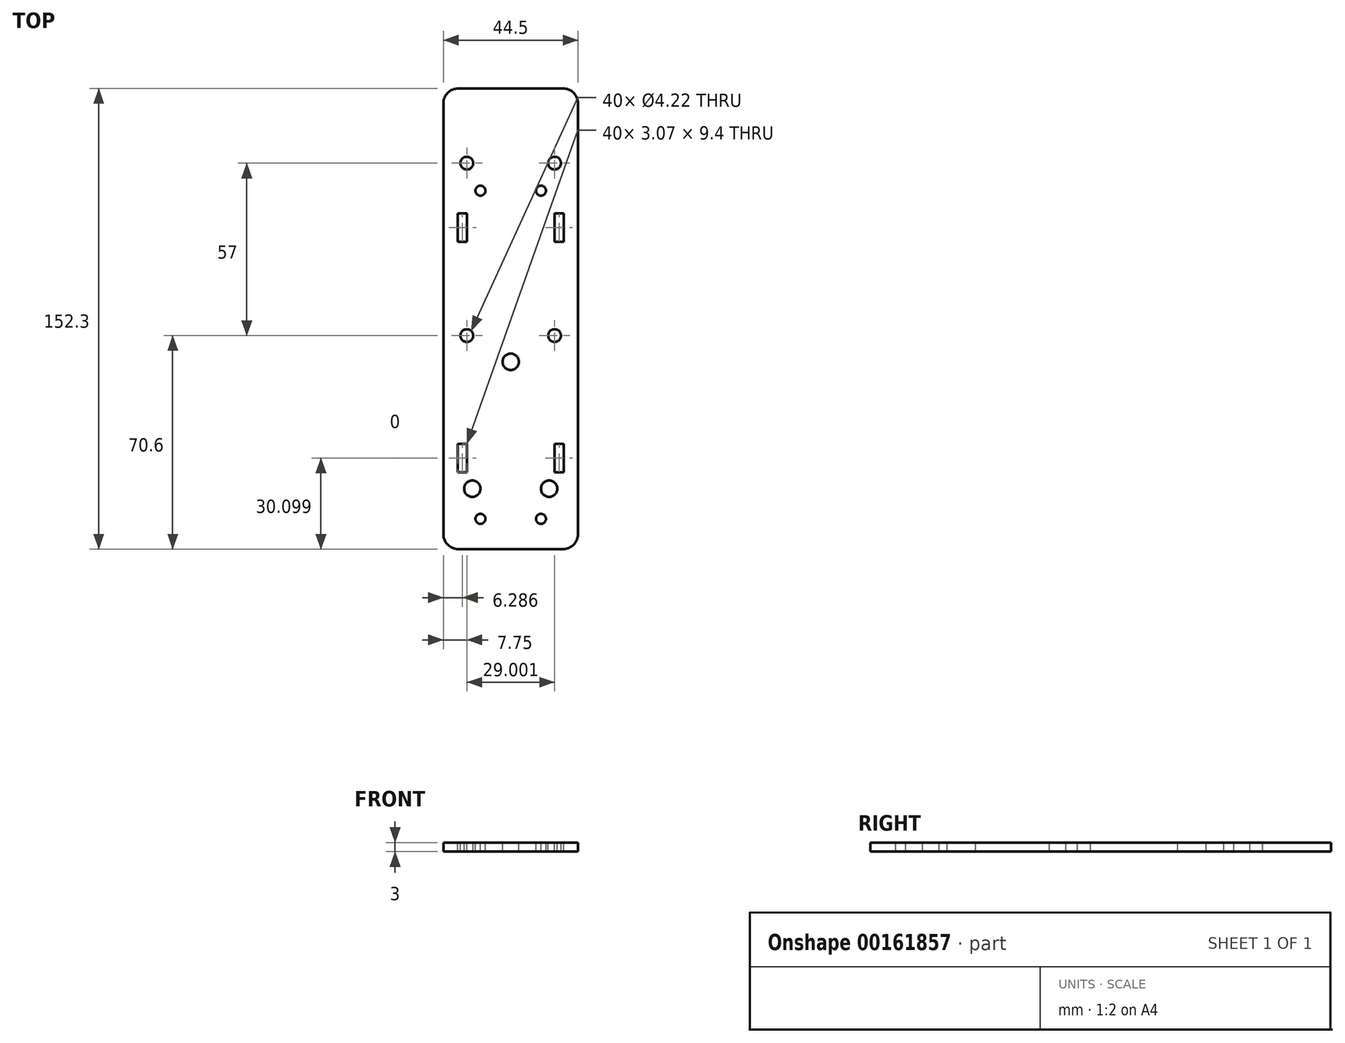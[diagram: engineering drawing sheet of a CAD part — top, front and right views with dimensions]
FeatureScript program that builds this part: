
annotation { "Feature Type Name" : "Feature", "Feature Type Description" : "" }
export const myFeature = defineFeature(function(context is Context, id is Id, definition is map)
    precondition{}
    {
        {
            var Q0;
            Q0=qCreatedBy(makeId("Top.planeOp"),FACE);
            var sketch = newSketch(context, id + "F0", { "sketchPlane" : qUnion([Q0])});
            skLineSegment(sketch, "E0.bottom", {"start": v(17.25, -78) * mm, "end": v(-17.25, -78) * mm});
            skLineSegment(sketch, "E0.top", {"start": v(17.25, 78) * mm, "end": v(-17.25, 78) * mm});
            skLineSegment(sketch, "E0.left", {"start": v(22.25, -73) * mm, "end": v(22.25, 73) * mm});
            skLineSegment(sketch, "E0.right", {"start": v(-22.25, -73) * mm, "end": v(-22.25, 73) * mm});
            skPoint(sketch, "E0.middle", {"position": v(0, 0) * mm});
            skPoint(sketch, "E1.visualSharp", {"position": v(-22.25, -78) * mm});
            skArc(sketch, "E1.filletArc", {"start": v(-22.25, -73) * mm, "mid": v(-20.79, -76.54) * mm, "end": v(-17.25, -78) * mm});
            skPoint(sketch, "E2.visualSharp", {"position": v(22.25, -78) * mm});
            skArc(sketch, "E2.filletArc", {"start": v(17.25, -78) * mm, "mid": v(20.79, -76.54) * mm, "end": v(22.25, -73) * mm});
            skPoint(sketch, "E3.visualSharp", {"position": v(-22.25, 78) * mm});
            skArc(sketch, "E3.filletArc", {"start": v(-17.25, 78) * mm, "mid": v(-20.79, 76.54) * mm, "end": v(-22.25, 73) * mm});
            skPoint(sketch, "E4.visualSharp", {"position": v(22.25, 78) * mm});
            skArc(sketch, "E4.filletArc", {"start": v(22.25, 73) * mm, "mid": v(20.79, 76.54) * mm, "end": v(17.25, 78) * mm});
            skSolve(sketch);
        }
        {
            var Q0;
            Q0=qSketchRegion(id+"F0",true);
            extrude(context, id + "F1", {"entities" : qUnion([Q0]), "oppositeDirection" : true, "depth" : 3 * mm});
        }
        {
            var Q0;
            Q0=makeQuery(id+"F1.opExtrude","CAP_FACE",FACE,{"disambiguationData":[OSD([sQuery(id+"F0.wireOp",EDGE,"E0.bottom"),sQuery(id+"F0.wireOp",EDGE,"E0.top"),sQuery(id+"F0.wireOp",EDGE,"E0.left"),sQuery(id+"F0.wireOp",EDGE,"E0.right"),sQuery(id+"F0.wireOp",EDGE,"E1.filletArc"),sQuery(id+"F0.wireOp",EDGE,"E2.filletArc"),sQuery(id+"F0.wireOp",EDGE,"E3.filletArc"),sQuery(id+"F0.wireOp",EDGE,"E4.filletArc")])],"isStart":true});
            var sketch = newSketch(context, id + "F2", { "sketchPlane" : qUnion([Q0])});
            skLineSegment(sketch, "E5.0", {"start": v(17.25, 78) * mm, "end": v(-17.25, 78) * mm});
            skLineSegment(sketch, "E5.1", {"start": v(-22.25, -73) * mm, "end": v(-22.25, 73) * mm});
            skLineSegment(sketch, "E5.2", {"start": v(22.25, -73) * mm, "end": v(22.25, 73) * mm});
            skLineSegment(sketch, "E5.3", {"start": v(17.25, -78) * mm, "end": v(-17.25, -78) * mm});
            skCircle(sketch, "E6", {"center": v(-10, -68) * mm, "radius": 1.65 * mm});
            skCircle(sketch, "E7", {"center": v(-12.7, -58.02) * mm, "radius": 2.7 * mm});
            skCircle(sketch, "E8", {"center": v(-14.5, -7.4) * mm, "radius": 2.1 * mm});
            skCircle(sketch, "E9", {"center": v(-10, 40.5) * mm, "radius": 1.65 * mm});
            skCircle(sketch, "E10", {"center": v(-14.5, 49.6) * mm, "radius": 2.1 * mm});
            skLineSegment(sketch, "E11", {"start": v(0, -78) * mm, "end": v(0, 78) * mm});
            skCircle(sketch, "E12.MirrorC", {"center": v(10, -68) * mm, "radius": 1.65 * mm});
            skCircle(sketch, "E13.MirrorC", {"center": v(12.7, -58.02) * mm, "radius": 2.7 * mm});
            skCircle(sketch, "E14.MirrorC", {"center": v(14.5, -7.4) * mm, "radius": 2.1 * mm});
            skCircle(sketch, "E15.MirrorC", {"center": v(10, 40.5) * mm, "radius": 1.65 * mm});
            skCircle(sketch, "E16.MirrorC", {"center": v(14.5, 49.6) * mm, "radius": 2.1 * mm});
            skCircle(sketch, "E17", {"center": v(0, -16.08) * mm, "radius": 2.7 * mm});
            skLineSegment(sketch, "E18.bottom", {"start": v(-17.5, -52.6) * mm, "end": v(-14.43, -52.6) * mm});
            skLineSegment(sketch, "E18.top", {"start": v(-17.5, -43.2) * mm, "end": v(-14.43, -43.2) * mm});
            skLineSegment(sketch, "E18.left", {"start": v(-17.5, -52.6) * mm, "end": v(-17.5, -43.2) * mm});
            skLineSegment(sketch, "E18.right", {"start": v(-14.43, -52.6) * mm, "end": v(-14.43, -43.2) * mm});
            skLineSegment(sketch, "E19.bottom", {"start": v(-17.5, 23.6) * mm, "end": v(-14.43, 23.6) * mm});
            skLineSegment(sketch, "E19.left", {"start": v(-17.5, 23.6) * mm, "end": v(-17.5, 33) * mm});
            skLineSegment(sketch, "E19.right", {"start": v(-14.43, 23.6) * mm, "end": v(-14.43, 33) * mm});
            skLineSegment(sketch, "E20", {"start": v(-14.43, 33) * mm, "end": v(-17.5, 33) * mm});
            skLineSegment(sketch, "E21.MirrorCS", {"start": v(17.5, 23.6) * mm, "end": v(14.43, 23.6) * mm});
            skLineSegment(sketch, "E22.MirrorCS", {"start": v(14.43, 23.6) * mm, "end": v(14.43, 33) * mm});
            skLineSegment(sketch, "E23.MirrorCS", {"start": v(14.43, 33) * mm, "end": v(17.5, 33) * mm});
            skLineSegment(sketch, "E24.MirrorCS", {"start": v(17.5, 23.6) * mm, "end": v(17.5, 33) * mm});
            skLineSegment(sketch, "E25.MirrorCS", {"start": v(14.43, -52.6) * mm, "end": v(14.43, -43.2) * mm});
            skLineSegment(sketch, "E26.MirrorCS", {"start": v(17.5, -43.2) * mm, "end": v(14.43, -43.2) * mm});
            skLineSegment(sketch, "E27.MirrorCS", {"start": v(17.5, -52.6) * mm, "end": v(17.5, -43.2) * mm});
            skLineSegment(sketch, "E28.MirrorCS", {"start": v(17.5, -52.6) * mm, "end": v(14.43, -52.6) * mm});
            skSolve(sketch);
        }
        {
            var Q0;
            Q0=qSketchRegion(id+"F2",true);
            extrude(context, id + "F3", {"entities" : qUnion([Q0]), "operationType" : NewBodyOperationType.REMOVE, "endBound" : BoundingType.THROUGH_ALL, "oppositeDirection" : true, "depth" : 25.4 * mm});
        }
        {
            var Q0;
            Q0=makeQuery(id+"F1.opExtrude","CAP_FACE",FACE,{"disambiguationData":[OSD([sQuery(id+"F0.wireOp",EDGE,"E0.bottom"),sQuery(id+"F0.wireOp",EDGE,"E0.top"),sQuery(id+"F0.wireOp",EDGE,"E0.left"),sQuery(id+"F0.wireOp",EDGE,"E0.right"),sQuery(id+"F0.wireOp",EDGE,"E1.filletArc"),sQuery(id+"F0.wireOp",EDGE,"E2.filletArc"),sQuery(id+"F0.wireOp",EDGE,"E3.filletArc"),sQuery(id+"F0.wireOp",EDGE,"E4.filletArc")])],"isStart":true});
            var sketch = newSketch(context, id + "F4", { "sketchPlane" : qUnion([Q0])});
            skLineSegment(sketch, "E29", {"start": v(-17.25, 74.3) * mm, "end": v(17.25, 74.3) * mm});
            skLineSegment(sketch, "E30.0", {"start": v(-22.25, -73) * mm, "end": v(-22.25, 69.3) * mm});
            skLineSegment(sketch, "E30.1", {"start": v(17.25, 78) * mm, "end": v(-17.25, 78) * mm});
            skLineSegment(sketch, "E30.2", {"start": v(22.25, -73) * mm, "end": v(22.25, 69.3) * mm});
            skPoint(sketch, "E31.newPointA", {"position": v(-22.25, 73) * mm});
            skArc(sketch, "E31.filletArc", {"start": v(-17.25, 74.3) * mm, "mid": v(-20.79, 72.83) * mm, "end": v(-22.25, 69.3) * mm});
            skPoint(sketch, "E32.newPointB", {"position": v(22.25, 73) * mm});
            skArc(sketch, "E32.filletArc", {"start": v(22.25, 69.3) * mm, "mid": v(20.79, 72.83) * mm, "end": v(17.25, 74.3) * mm});
            skSolve(sketch);
        }
        {
            var Q0;
            Q0=qSketchRegion(id+"F4",true);
            var Q1;
            Q1=makeQuery(id+"F4.imprint","IMPRINT",FACE,{"disambiguationData":[TD([[makeQuery(id+"F4.imprint","IMPRINT",EDGE,{"derivedFrom":sQuery(id+"F4.wireOp",EDGE,"E29")}),1.0]])]});
            extrude(context, id + "F5", {"entities" : qUnion([Q0, Q1]), "operationType" : NewBodyOperationType.REMOVE, "endBound" : BoundingType.THROUGH_ALL, "oppositeDirection" : true, "depth" : 25.4 * mm});
        }
    });
